# Revit family: LIANO II - FREESTANDING BATH FILLER
name_source: partatom
category: Plumbing Fixtures
units: mm (PartAtom-declared; Revit-internal decimal feet)

## family parameters
Cut with Voids When Loaded = No
Host = Face
OmniClass Number = 23.45.55.14
OmniClass Title = Single Faucets
Part Type = Normal
Room Calculation Point = No
Round Connector Dimension = Use Diameter
Shared = No

## types (5) — shared parameters
Assembly Code = C1030220
CW Connection = Yes
HW Connection = Yes
Manufacturer = GWA Bathrooms & Kitchens
Overall_Height = 850 mm  [stored 2.78871 ft]
StemHeight = 686 mm  [stored 2.25066 ft]
URL = https://www.caroma.com.au
Vent Connection = No
Waste Connection = No
zero-valued in all types: Default Elevation

## per-type parameters (varying)
| type | Material_Base | Model |
| LIANO II - FREESTANDING BATH FILLER - Chrome | GWA_Metal-Chrome | 96378C |
| LIANO II - FREESTANDING BATH FILLER - Matte Black | GWA-Metal-Black | 96378B |
| LIANO II - FREESTANDING BATH FILLER - Brass | GWA_Metal-Brushed-Brass | 96378BB |
| LIANO II - FREESTANDING BATH FILLER - Gunmetal | GWA-Metal-Gunmetal Grey | 96378GM |
| LIANO II - FREESTANDING BATH FILLER - Brushed Nickel | GWA_Metal-Brushed-Nickel | 96378BN |

note: column(s) folded — value = type name in every type: Description

note: [stored X ft] marks values corroborated as IEEE doubles in the binary element streams (Revit-internal decimal feet)

## geometry (parser evidence)
native form markers: Sweep x2
no freeform markers — native parametric forms only
